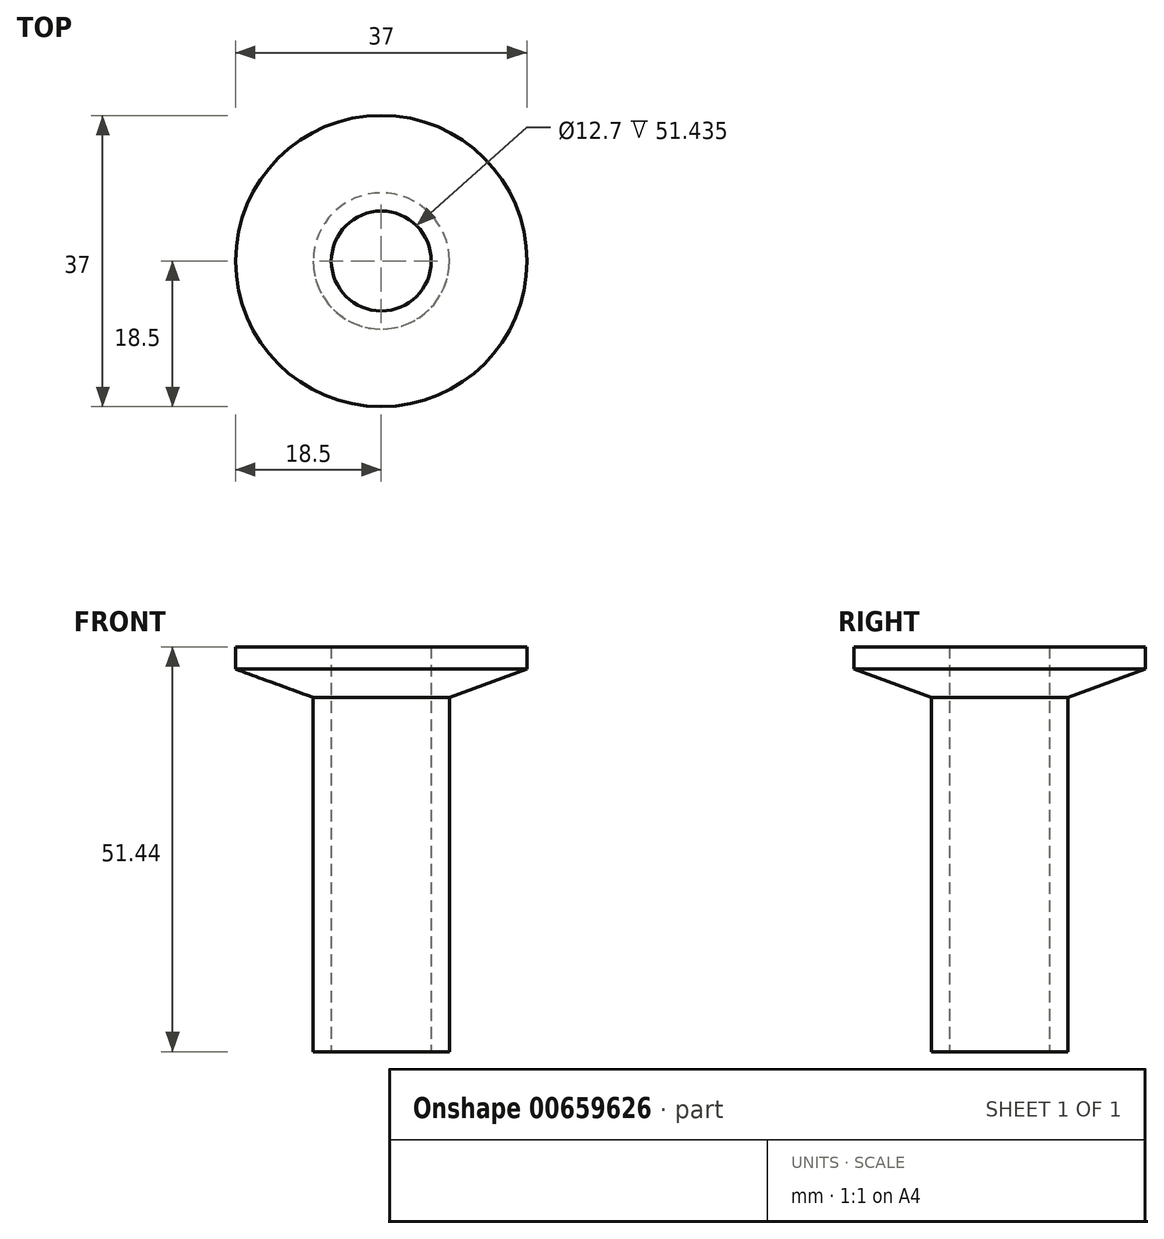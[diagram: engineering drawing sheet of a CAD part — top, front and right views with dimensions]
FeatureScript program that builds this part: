
annotation { "Feature Type Name" : "Feature", "Feature Type Description" : "" }
export const myFeature = defineFeature(function(context is Context, id is Id, definition is map)
    precondition{}
    {
        {
            var Q0;
            Q0=qCreatedBy(makeId("Front.planeOp"),FACE);
            var sketch = newSketch(context, id + "F0", { "sketchPlane" : qUnion([Q0])});
            skLineSegment(sketch, "E0", {"start": v(6.35, 0) * mm, "end": v(6.35, 6.44) * mm});
            skLineSegment(sketch, "E1", {"start": v(6.35, 6.44) * mm, "end": v(18.5, 6.44) * mm});
            skLineSegment(sketch, "E2", {"start": v(18.5, 6.44) * mm, "end": v(18.5, 3.59) * mm});
            skLineSegment(sketch, "E3", {"start": v(18.5, 3.59) * mm, "end": v(8.65, 0) * mm});
            skLineSegment(sketch, "E4", {"start": v(8.65, 0) * mm, "end": v(6.35, 0) * mm});
            skLineSegment(sketch, "E5", {"start": v(0, 0) * mm, "end": v(0, 11.29) * mm, "construction": true});
            skSolve(sketch);
        }
        {
            var Q0;
            Q0=qSketchRegion(id+"F0",true);
            var Q1;
            Q1=sQuery(id+"F0.wireOp",EDGE,"E5");
            revolve(context, id + "F1", {"entities" : qUnion([Q0]), "axis" : qUnion([Q1]), "revolveType" : RevolveType.FULL});
        }
        {
            var Q0;
            Q0=qCreatedBy(makeId("Top.planeOp"),FACE);
            var sketch = newSketch(context, id + "F2", { "sketchPlane" : qUnion([Q0])});
            skCircle(sketch, "E6", {"center": v(0, 0) * mm, "radius": 8.65 * mm});
            skCircle(sketch, "E7", {"center": v(0, 0) * mm, "radius": 6.35 * mm});
            skSolve(sketch);
        }
        {
            var Q0;
            Q0=qSketchRegion(id+"F2",true);
            extrude(context, id + "F3", {"entities" : qUnion([Q0]), "operationType" : NewBodyOperationType.ADD, "oppositeDirection" : true, "depth" : 45 * mm, "offsetDistance" : 25 * mm});
        }
    });
